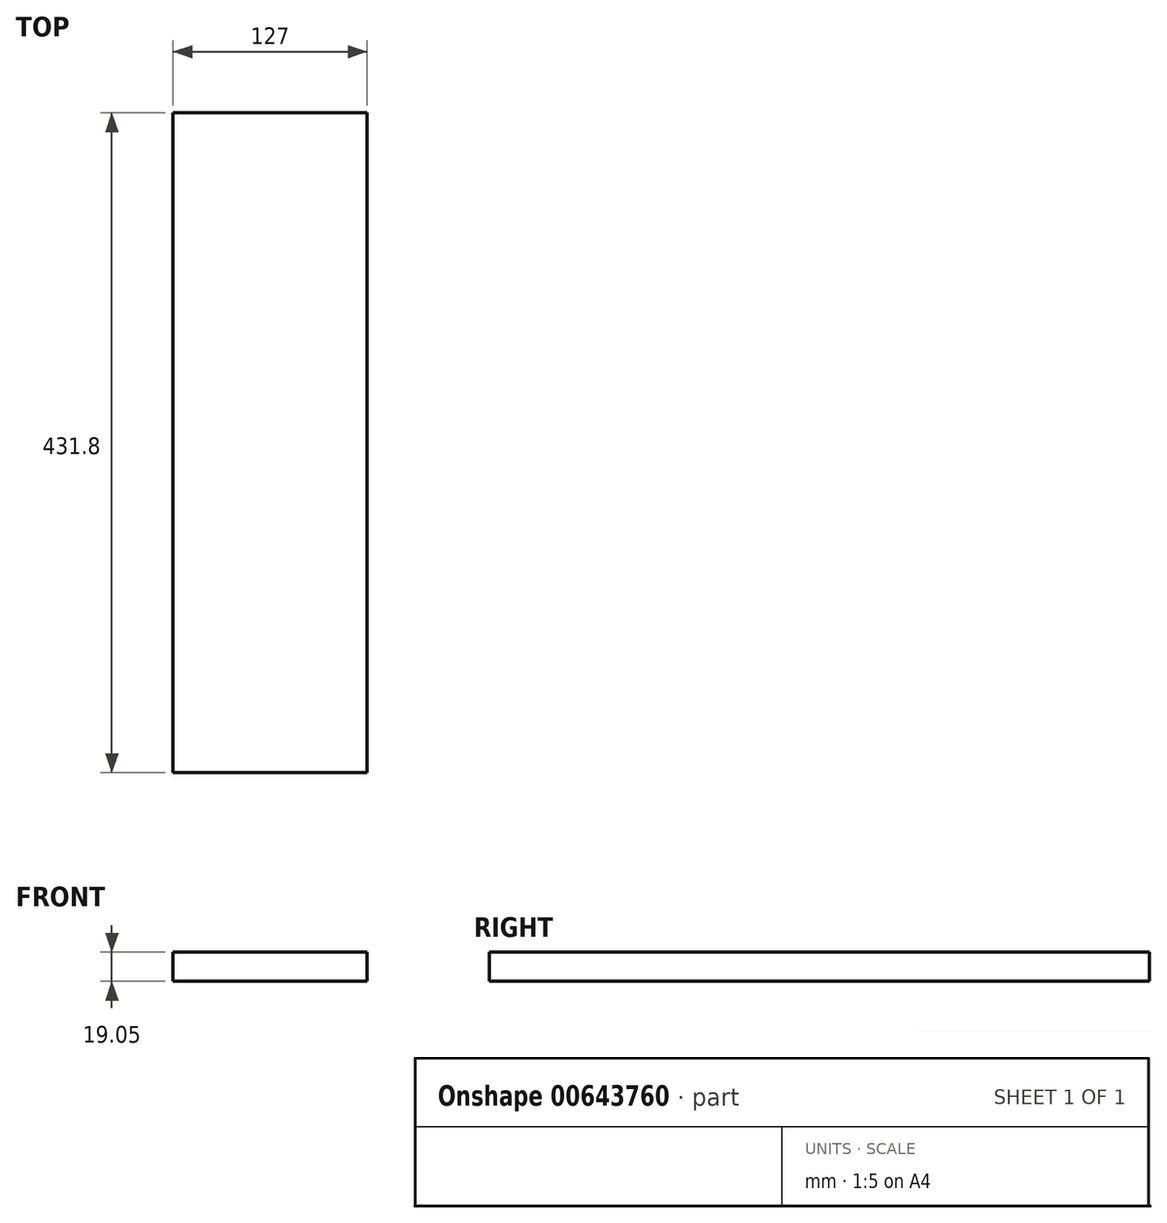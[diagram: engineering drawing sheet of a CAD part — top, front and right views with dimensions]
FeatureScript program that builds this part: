
annotation { "Feature Type Name" : "Feature", "Feature Type Description" : "" }
export const myFeature = defineFeature(function(context is Context, id is Id, definition is map)
    precondition{}
    {
        {
            var Q0;
            Q0=qCreatedBy(makeId("Top.planeOp"),FACE);
            var sketch = newSketch(context, id + "F0", { "sketchPlane" : qUnion([Q0])});
            skLineSegment(sketch, "E0.bottom", {"start": v(0, 0) * mm, "end": v(127, 0) * mm});
            skLineSegment(sketch, "E0.top", {"start": v(0, -431.8) * mm, "end": v(127, -431.8) * mm});
            skLineSegment(sketch, "E0.left", {"start": v(0, 0) * mm, "end": v(0, -431.8) * mm});
            skLineSegment(sketch, "E0.right", {"start": v(127, 0) * mm, "end": v(127, -431.8) * mm});
            skSolve(sketch);
        }
        {
            var Q0;
            Q0 = qSketchRegion(id + "F0", true);
            extrude(context, id + "F1", {"entities" : qUnion([Q0]), "depth" : 19.05 * mm, "offsetDistance" : 25.4 * mm});
        }
    });
